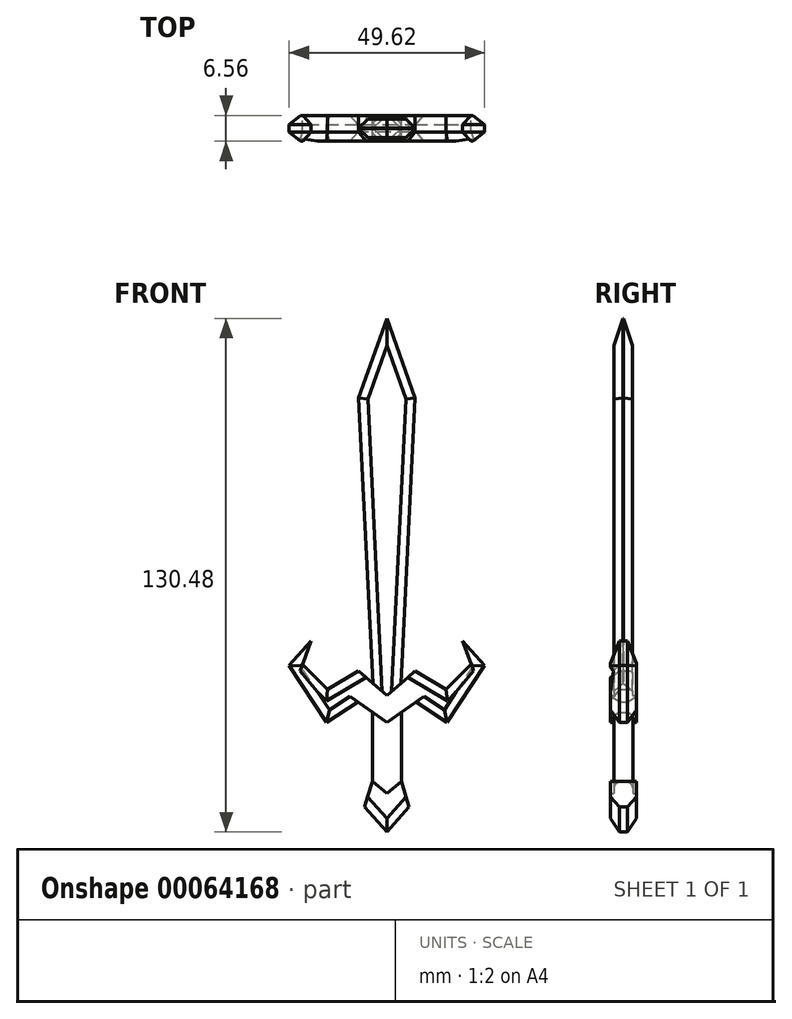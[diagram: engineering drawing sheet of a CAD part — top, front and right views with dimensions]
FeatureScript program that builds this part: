
annotation { "Feature Type Name" : "Feature", "Feature Type Description" : "" }
export const myFeature = defineFeature(function(context is Context, id is Id, definition is map)
    precondition{}
    {
        {
            var Q0;
            Q0=qCreatedBy(makeId("Front.planeOp"),FACE);
            var sketch = newSketch(context, id + "F0", { "sketchPlane" : qUnion([Q0])});
            skLineSegment(sketch, "E0", {"start": v(0, -34.22) * mm, "end": v(7.39, -29.05) * mm});
            skLineSegment(sketch, "E1", {"start": v(7.39, -29.05) * mm, "end": v(15.26, -34.22) * mm});
            skLineSegment(sketch, "E2", {"start": v(15.26, -34.22) * mm, "end": v(24.81, -19.67) * mm});
            skLineSegment(sketch, "E3", {"start": v(24.81, -19.67) * mm, "end": v(19.2, -13.54) * mm});
            skLineSegment(sketch, "E4", {"start": v(19.2, -13.54) * mm, "end": v(21.42, -19.45) * mm});
            skLineSegment(sketch, "E5", {"start": v(21.42, -19.45) * mm, "end": v(15.02, -25.85) * mm});
            skLineSegment(sketch, "E6", {"start": v(15.02, -25.85) * mm, "end": v(7.14, -21.17) * mm});
            skLineSegment(sketch, "E7", {"start": v(7.14, -21.17) * mm, "end": v(0, -27.33) * mm});
            skLineSegment(sketch, "E8.MirrorCS", {"start": v(0, -34.22) * mm, "end": v(-7.39, -29.05) * mm});
            skLineSegment(sketch, "E9.MirrorCS", {"start": v(-7.14, -21.17) * mm, "end": v(0, -27.33) * mm});
            skLineSegment(sketch, "E10.MirrorCS", {"start": v(-15.02, -25.85) * mm, "end": v(-7.14, -21.17) * mm});
            skLineSegment(sketch, "E11.MirrorCS", {"start": v(-7.39, -29.05) * mm, "end": v(-15.26, -34.22) * mm});
            skLineSegment(sketch, "E12.MirrorCS", {"start": v(-15.26, -34.22) * mm, "end": v(-24.81, -19.67) * mm});
            skLineSegment(sketch, "E13.MirrorCS", {"start": v(-21.42, -19.45) * mm, "end": v(-15.02, -25.85) * mm});
            skLineSegment(sketch, "E14.MirrorCS", {"start": v(-24.81, -19.67) * mm, "end": v(-19.2, -13.54) * mm});
            skLineSegment(sketch, "E15.MirrorCS", {"start": v(-19.2, -13.54) * mm, "end": v(-21.42, -19.45) * mm});
            skLineSegment(sketch, "E16", {"start": v(3.57, -24.25) * mm, "end": v(7.14, 48.25) * mm});
            skLineSegment(sketch, "E17", {"start": v(7.14, 48.25) * mm, "end": v(0, 68.44) * mm});
            skLineSegment(sketch, "E18.MirrorCS", {"start": v(-7.14, 48.25) * mm, "end": v(0, 68.44) * mm});
            skLineSegment(sketch, "E19.MirrorCS", {"start": v(-3.57, -24.25) * mm, "end": v(-7.14, 48.25) * mm});
            skLineSegment(sketch, "E20", {"start": v(3.7, -31.63) * mm, "end": v(3.7, -49.24) * mm});
            skLineSegment(sketch, "E21", {"start": v(3.7, -49.24) * mm, "end": v(0, -52.2) * mm});
            skLineSegment(sketch, "E22", {"start": v(3.7, -49.24) * mm, "end": v(5.66, -55.64) * mm});
            skLineSegment(sketch, "E23", {"start": v(5.66, -55.64) * mm, "end": v(0, -62.04) * mm});
            skLineSegment(sketch, "E24.MirrorCS", {"start": v(-5.66, -55.64) * mm, "end": v(0, -62.04) * mm});
            skLineSegment(sketch, "E25.MirrorCS", {"start": v(-3.7, -31.63) * mm, "end": v(-3.7, -49.24) * mm});
            skLineSegment(sketch, "E26.MirrorCS", {"start": v(-3.7, -49.24) * mm, "end": v(0, -52.2) * mm});
            skLineSegment(sketch, "E27.MirrorCS", {"start": v(-3.7, -49.24) * mm, "end": v(-5.66, -55.64) * mm});
            skPoint(sketch, "E28.start.orphan", {"position": v(0, -76.07) * mm});
            skSolve(sketch);
        }
        {
            var Q0;
            {var subQ0=sQuery(id+"F0.wireOp",EDGE,"E16");Q0=makeQuery(id+"F0.imprint","IMPRINT",FACE,{"disambiguationData":[TD([[makeQuery(id+"F0.imprint","IMPRINT",EDGE,{"derivedFrom":subQ0}),1.0]])]});}
            extrude(context, id + "F1", {"entities" : qUnion([Q0]), "endBound" : BoundingType.SYMMETRIC, "depth" : 4.66 * mm});
        }
        {
            var Q0;
            Q0=makeQuery(id+"F1.opExtrude","CAP_EDGE",EDGE,{"disambiguationData":[OSD([sQuery(id+"F0.wireOp",EDGE,"E19.MirrorCS")])],"isStart":false});
            var Q1;
            Q1=makeQuery(id+"F1.opExtrude","CAP_EDGE",EDGE,{"disambiguationData":[OSD([sQuery(id+"F0.wireOp",EDGE,"E16")])],"isStart":false});
            var Q2;
            Q2=makeQuery(id+"F1.opExtrude","CAP_EDGE",EDGE,{"disambiguationData":[OSD([sQuery(id+"F0.wireOp",EDGE,"E18.MirrorCS")])],"isStart":false});
            var Q3;
            Q3=makeQuery(id+"F1.opExtrude","CAP_EDGE",EDGE,{"disambiguationData":[OSD([sQuery(id+"F0.wireOp",EDGE,"E17")])],"isStart":false});
            var Q4;
            Q4=makeQuery(id+"F1.opExtrude","CAP_EDGE",EDGE,{"disambiguationData":[OSD([sQuery(id+"F0.wireOp",EDGE,"E18.MirrorCS")])],"isStart":true});
            var Q5;
            Q5=makeQuery(id+"F1.opExtrude","CAP_EDGE",EDGE,{"disambiguationData":[OSD([sQuery(id+"F0.wireOp",EDGE,"E17")])],"isStart":true});
            var Q6;
            Q6=makeQuery(id+"F1.opExtrude","CAP_EDGE",EDGE,{"disambiguationData":[OSD([sQuery(id+"F0.wireOp",EDGE,"E16")])],"isStart":true});
            var Q7;
            Q7=makeQuery(id+"F1.opExtrude","CAP_EDGE",EDGE,{"disambiguationData":[OSD([sQuery(id+"F0.wireOp",EDGE,"E19.MirrorCS")])],"isStart":true});
            chamfer(context, id + "F2", {"entities" : qUnion([Q0, Q1, Q2, Q3, Q4, Q5, Q6, Q7]), "width" : 2.3 * mm, "tangentPropagation" : true});
        }
        {
            var Q0;
            {var subQ8=sQuery(id+"F0.wireOp",EDGE,"E1");Q0=makeQuery(id+"F0.imprint","IMPRINT",FACE,{"disambiguationData":[TD([[makeQuery(id+"F0.imprint","IMPRINT",EDGE,{"derivedFrom":subQ8}),1.0]])]});}
            extrude(context, id + "F3", {"entities" : qUnion([Q0]), "operationType" : NewBodyOperationType.ADD, "endBound" : BoundingType.SYMMETRIC, "depth" : 6.56 * mm});
        }
        {
            var Q0;
            Q0=makeQuery(id+"F3.opExtrude","CAP_EDGE",EDGE,{"disambiguationData":[OSD([sQuery(id+"F0.wireOp",EDGE,"E12.MirrorCS")])],"isStart":false});
            var Q1;
            Q1=makeQuery(id+"F3.opExtrude","CAP_EDGE",EDGE,{"disambiguationData":[OSD([sQuery(id+"F0.wireOp",EDGE,"E11.MirrorCS")])],"isStart":false});
            var Q2;
            Q2=makeQuery(id+"F3.opExtrude","CAP_EDGE",EDGE,{"disambiguationData":[OSD([sQuery(id+"F0.wireOp",EDGE,"E1")])],"isStart":false});
            var Q3;
            Q3=makeQuery(id+"F3.opExtrude","CAP_EDGE",EDGE,{"disambiguationData":[OSD([sQuery(id+"F0.wireOp",EDGE,"E2")])],"isStart":false});
            var Q4;
            Q4=makeQuery(id+"F3.opExtrude","CAP_EDGE",EDGE,{"disambiguationData":[OSD([sQuery(id+"F0.wireOp",EDGE,"E12.MirrorCS")])],"isStart":true});
            var Q5;
            Q5=makeQuery(id+"F3.opExtrude","CAP_EDGE",EDGE,{"disambiguationData":[OSD([sQuery(id+"F0.wireOp",EDGE,"E11.MirrorCS")])],"isStart":true});
            var Q6;
            Q6=makeQuery(id+"F3.opExtrude","CAP_EDGE",EDGE,{"disambiguationData":[OSD([sQuery(id+"F0.wireOp",EDGE,"E2")])],"isStart":true});
            var Q7;
            Q7=makeQuery(id+"F3.opExtrude","CAP_EDGE",EDGE,{"disambiguationData":[OSD([sQuery(id+"F0.wireOp",EDGE,"E1")])],"isStart":true});
            var Q8;
            Q8=makeQuery(id+"F3.opExtrude","CAP_EDGE",EDGE,{"disambiguationData":[OSD([sQuery(id+"F0.wireOp",EDGE,"E14.MirrorCS")])],"isStart":true});
            var Q9;
            Q9=makeQuery(id+"F3.opExtrude","CAP_EDGE",EDGE,{"disambiguationData":[OSD([sQuery(id+"F0.wireOp",EDGE,"E14.MirrorCS")])],"isStart":false});
            var Q10;
            Q10=makeQuery(id+"F3.opExtrude","CAP_EDGE",EDGE,{"disambiguationData":[OSD([sQuery(id+"F0.wireOp",EDGE,"E3")])],"isStart":true});
            var Q11;
            Q11=makeQuery(id+"F3.opExtrude","CAP_EDGE",EDGE,{"disambiguationData":[OSD([sQuery(id+"F0.wireOp",EDGE,"E3")])],"isStart":false});
            var Q12;
            Q12=makeQuery(id+"F3.opExtrude","CAP_EDGE",EDGE,{"disambiguationData":[OSD([sQuery(id+"F0.wireOp",EDGE,"E5")])],"isStart":false});
            var Q13;
            Q13=makeQuery(id+"F3.opExtrude","CAP_EDGE",EDGE,{"disambiguationData":[OSD([sQuery(id+"F0.wireOp",EDGE,"E6")])],"isStart":false});
            var Q14;
            Q14=makeQuery(id+"F3.opExtrude","CAP_EDGE",EDGE,{"disambiguationData":[OSD([sQuery(id+"F0.wireOp",EDGE,"E10.MirrorCS")])],"isStart":false});
            var Q15;
            Q15=makeQuery(id+"F3.opExtrude","CAP_EDGE",EDGE,{"disambiguationData":[OSD([sQuery(id+"F0.wireOp",EDGE,"E13.MirrorCS")])],"isStart":false});
            chamfer(context, id + "F4", {"entities" : qUnion([Q0, Q1, Q2, Q3, Q4, Q5, Q6, Q7, Q8, Q9, Q10, Q11, Q12, Q13, Q14, Q15]), "width" : 2.3 * mm, "tangentPropagation" : true});
        }
        {
            var Q0;
            {var subQ0=sQuery(id+"F0.wireOp",EDGE,"E20");Q0=makeQuery(id+"F0.imprint","IMPRINT",FACE,{"disambiguationData":[TD([[makeQuery(id+"F0.imprint","IMPRINT",EDGE,{"derivedFrom":subQ0}),-1.0]])]});}
            extrude(context, id + "F5", {"entities" : qUnion([Q0]), "operationType" : NewBodyOperationType.ADD, "endBound" : BoundingType.SYMMETRIC, "depth" : 4.8 * mm});
        }
        {
            var Q0;
            Q0=makeQuery(id+"F5.opExtrude","CAP_EDGE",EDGE,{"disambiguationData":[OSD([sQuery(id+"F0.wireOp",EDGE,"E25.MirrorCS")])],"isStart":true});
            var Q1;
            Q1=makeQuery(id+"F5.opExtrude","CAP_EDGE",EDGE,{"disambiguationData":[OSD([sQuery(id+"F0.wireOp",EDGE,"E25.MirrorCS")])],"isStart":false});
            var Q2;
            Q2=makeQuery(id+"F5.opExtrude","CAP_EDGE",EDGE,{"disambiguationData":[OSD([sQuery(id+"F0.wireOp",EDGE,"E20")])],"isStart":false});
            var Q3;
            Q3=makeQuery(id+"F5.opExtrude","CAP_EDGE",EDGE,{"disambiguationData":[OSD([sQuery(id+"F0.wireOp",EDGE,"E20")])],"isStart":true});
            fillet(context, id + "F6", {"entities" : qUnion([Q0, Q1, Q2, Q3]), "radius" : 2.03 * mm, "tangentPropagation" : true, "allowEdgeOverflow" : false});
        }
        {
            var Q0;
            Q0=makeQuery(id+"F0.imprint","IMPRINT",FACE,{"disambiguationData":[TD([[makeQuery(id+"F0.imprint","IMPRINT",EDGE,{"derivedFrom":sQuery(id+"F0.wireOp",EDGE,"E21")}),1.0]])]});
            extrude(context, id + "F7", {"entities" : qUnion([Q0]), "operationType" : NewBodyOperationType.ADD, "endBound" : BoundingType.SYMMETRIC, "depth" : 6.55 * mm});
        }
        {
            var Q0;
            Q0=makeQuery(id+"F7.opExtrude","CAP_EDGE",EDGE,{"disambiguationData":[OSD([sQuery(id+"F0.wireOp",EDGE,"E24.MirrorCS")])],"isStart":false});
            var Q1;
            Q1=makeQuery(id+"F7.opExtrude","CAP_EDGE",EDGE,{"disambiguationData":[OSD([sQuery(id+"F0.wireOp",EDGE,"E23")])],"isStart":false});
            var Q2;
            Q2=makeQuery(id+"F7.opExtrude","CAP_EDGE",EDGE,{"disambiguationData":[OSD([sQuery(id+"F0.wireOp",EDGE,"E24.MirrorCS")])],"isStart":true});
            var Q3;
            Q3=makeQuery(id+"F7.opExtrude","CAP_EDGE",EDGE,{"disambiguationData":[OSD([sQuery(id+"F0.wireOp",EDGE,"E23")])],"isStart":true});
            chamfer(context, id + "F8", {"entities" : qUnion([Q0, Q1, Q2, Q3]), "width" : 2.3 * mm, "tangentPropagation" : true});
        }
    });
